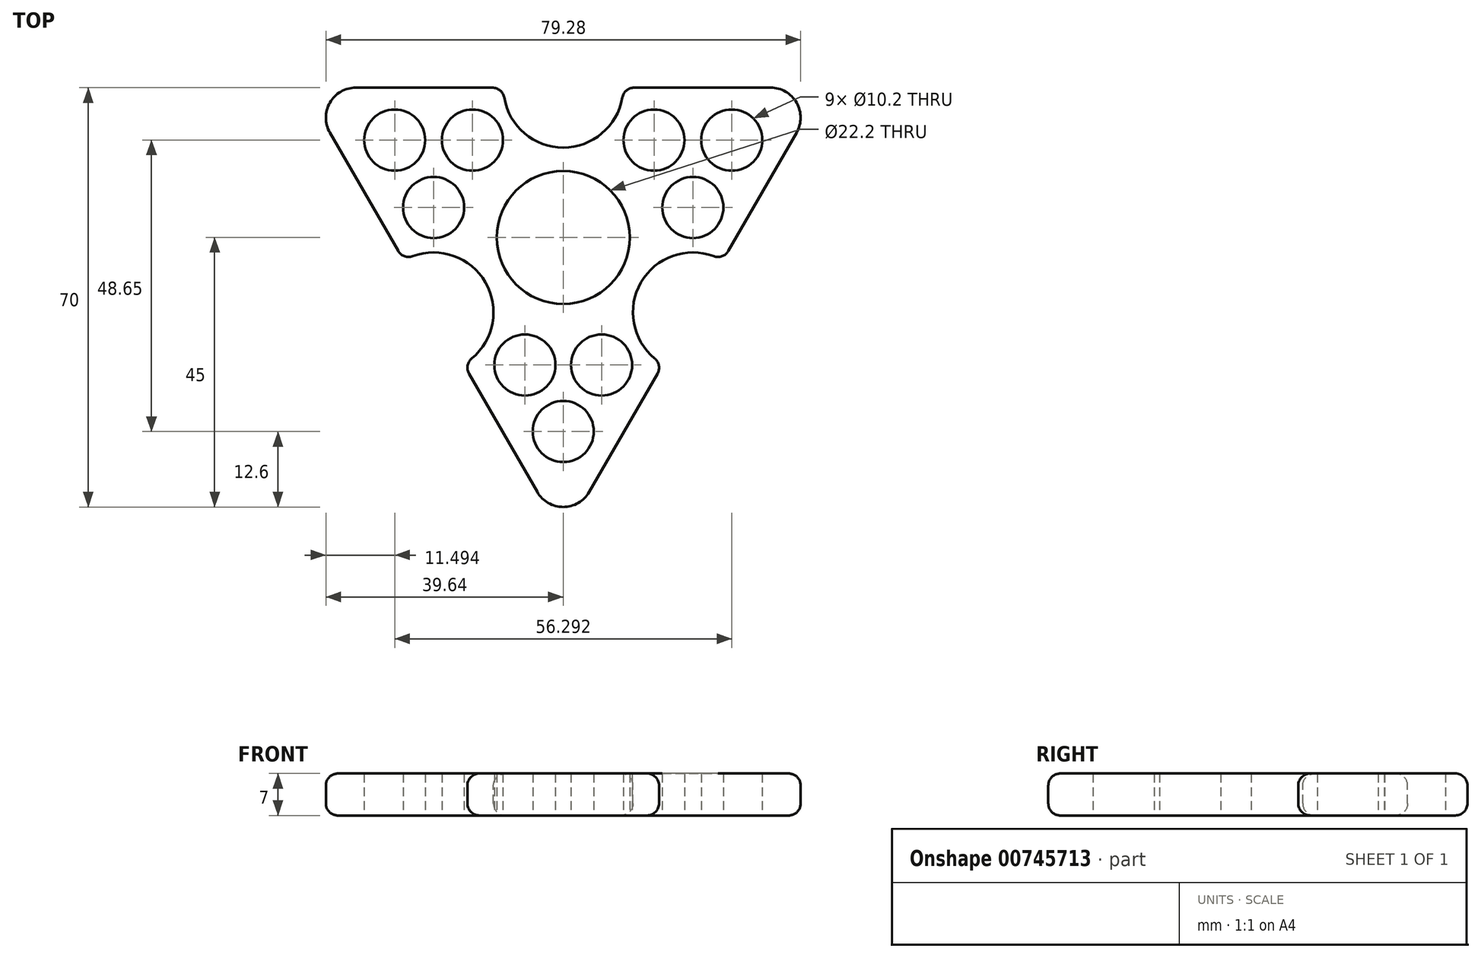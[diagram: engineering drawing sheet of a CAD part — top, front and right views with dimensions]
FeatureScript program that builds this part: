
annotation { "Feature Type Name" : "Feature", "Feature Type Description" : "" }
export const myFeature = defineFeature(function(context is Context, id is Id, definition is map)
    precondition{}
    {
        {
            var Q0;
            Q0=qCreatedBy(makeId("Top.planeOp"),FACE);
            var sketch = newSketch(context, id + "F0", { "sketchPlane" : qUnion([Q0])});
            skCircle(sketch, "E0", {"center": v(0, 0) * mm, "radius": 11.1 * mm});
            skCircle(sketch, "E1", {"center": v(0, -32.4) * mm, "radius": 5.1 * mm});
            skCircle(sketch, "E2.1.0", {"center": v(6.4, -21.3) * mm, "radius": 5.1 * mm});
            skCircle(sketch, "E2.2.0", {"center": v(-6.4, -21.3) * mm, "radius": 5.1 * mm});
            skPoint(sketch, "E2.center", {"position": v(0, -25) * mm});
            skCircle(sketch, "E3.1.1", {"center": v(28.15, 16.25) * mm, "radius": 5.1 * mm});
            skPoint(sketch, "E3.1.2", {"position": v(21.65, 12.5) * mm});
            skCircle(sketch, "E3.1.3", {"center": v(15.16, 16.25) * mm, "radius": 5.1 * mm});
            skCircle(sketch, "E3.1.4", {"center": v(21.65, 5) * mm, "radius": 5.1 * mm});
            skCircle(sketch, "E3.2.1", {"center": v(-28.15, 16.25) * mm, "radius": 5.1 * mm});
            skPoint(sketch, "E3.2.2", {"position": v(-21.65, 12.5) * mm});
            skCircle(sketch, "E3.2.3", {"center": v(-21.65, 5) * mm, "radius": 5.1 * mm});
            skCircle(sketch, "E3.2.4", {"center": v(-15.16, 16.25) * mm, "radius": 5.1 * mm});
            skLineSegment(sketch, "E4", {"start": v(0, 0) * mm, "end": v(0, -37.5) * mm});
            skPoint(sketch, "E5.orphan", {"position": v(0, -45) * mm});
            skPoint(sketch, "E6.orphan", {"position": v(-43.3, 25) * mm});
            skLineSegment(sketch, "E7", {"start": v(0, 0) * mm, "end": v(0, -50) * mm, "construction": true});
            skLineSegment(sketch, "E8", {"start": v(0, 0) * mm, "end": v(-43.3, 25) * mm, "construction": true});
            skLineSegment(sketch, "E9", {"start": v(0, -50) * mm, "end": v(-43.3, 25) * mm});
            skLineSegment(sketch, "E10.1.0", {"start": v(43.3, 25) * mm, "end": v(0, -50) * mm});
            skLineSegment(sketch, "E10.2.0", {"start": v(-43.3, 25) * mm, "end": v(43.3, 25) * mm});
            skSolve(sketch);
        }
        {
            var Q0;
            Q0=makeQuery(id+"F0.imprint","IMPRINT",FACE,{"disambiguationData":[TD([[makeQuery(id+"F0.imprint","IMPRINT",EDGE,{"derivedFrom":sQuery(id+"F0.wireOp",EDGE,"E0")}),-1.0]])]});
            extrude(context, id + "F1", {"entities" : qUnion([Q0]), "depth" : 7 * mm, "offsetDistance" : 25 * mm});
        }
        {
            var Q0;
            Q0=makeQuery(id+"F1.opExtrude","SWEPT_EDGE",EDGE,{"disambiguationData":[OSD([sQuery(id+"F0.wireOp",EDGE,"E9"),sQuery(id+"F0.wireOp",EDGE,"E10.2.0")])]});
            var Q1;
            Q1=makeQuery(id+"F1.opExtrude","SWEPT_EDGE",EDGE,{"disambiguationData":[OSD([sQuery(id+"F0.wireOp",EDGE,"E10.1.0"),sQuery(id+"F0.wireOp",EDGE,"E10.2.0")])]});
            var Q2;
            Q2=makeQuery(id+"F1.opExtrude","SWEPT_EDGE",EDGE,{"disambiguationData":[OSD([sQuery(id+"F0.wireOp",EDGE,"E9"),sQuery(id+"F0.wireOp",EDGE,"E10.1.0")])]});
            fillet(context, id + "F2", {"entities" : qUnion([Q0, Q1, Q2]), "radius" : 5 * mm, "tangentPropagation" : true, "allowEdgeOverflow" : false});
        }
        {
            var Q0;
            Q0=makeQuery(id+"F1.opExtrude","CAP_FACE",FACE,{"disambiguationData":[OSD([sQuery(id+"F0.wireOp",EDGE,"E0"),sQuery(id+"F0.wireOp",EDGE,"E1"),sQuery(id+"F0.wireOp",EDGE,"E2.1.0"),sQuery(id+"F0.wireOp",EDGE,"E2.2.0"),sQuery(id+"F0.wireOp",EDGE,"E3.1.1"),sQuery(id+"F0.wireOp",EDGE,"E3.1.3"),sQuery(id+"F0.wireOp",EDGE,"E3.1.4"),sQuery(id+"F0.wireOp",EDGE,"E3.2.1"),sQuery(id+"F0.wireOp",EDGE,"E3.2.3"),sQuery(id+"F0.wireOp",EDGE,"E3.2.4"),sQuery(id+"F0.wireOp",EDGE,"E9"),sQuery(id+"F0.wireOp",EDGE,"E10.1.0"),sQuery(id+"F0.wireOp",EDGE,"E10.2.0")])],"isStart":false});
            var sketch = newSketch(context, id + "F3", { "sketchPlane" : qUnion([Q0])});
            skCircle(sketch, "E11", {"center": v(0, 25) * mm, "radius": 10 * mm});
            skCircle(sketch, "E12.1.0", {"center": v(-21.65, -12.5) * mm, "radius": 10 * mm});
            skCircle(sketch, "E12.2.0", {"center": v(21.65, -12.5) * mm, "radius": 10 * mm});
            skPoint(sketch, "E12.center", {"position": v(0, 0) * mm});
            skSolve(sketch);
        }
        {
            var Q0;
            {var subQ0=sQuery(id+"F3.wireOp",EDGE,"E11");var subQ1=makeQuery(id+"F1.opExtrude","CAP_EDGE",EDGE,{"disambiguationData":[OSD([sQuery(id+"F0.wireOp",EDGE,"E10.2.0")])],"isStart":false});var subQ2=makeQuery(id+"F3.imprint","INTERSECT",VERTEX,{"disambiguationData":[OD(0.0)],"derivedFrom":[subQ1,subQ0]});Q0=makeQuery(id+"F3.imprint","IMPRINT",FACE,{"disambiguationData":[TD([[makeQuery(id+"F3.imprint","IMPRINT",EDGE,{"disambiguationData":[TD([[subQ2,-1.0]])],"derivedFrom":subQ0}),1.0]])]});}
            var Q1;
            {var subQ0=sQuery(id+"F3.wireOp",EDGE,"E12.1.0");var subQ1=makeQuery(id+"F1.opExtrude","CAP_EDGE",EDGE,{"disambiguationData":[OSD([sQuery(id+"F0.wireOp",EDGE,"E9")])],"isStart":false});var subQ2=makeQuery(id+"F3.imprint","INTERSECT",VERTEX,{"disambiguationData":[OD(0.0)],"derivedFrom":[subQ1,subQ0]});Q1=makeQuery(id+"F3.imprint","IMPRINT",FACE,{"disambiguationData":[TD([[makeQuery(id+"F3.imprint","IMPRINT",EDGE,{"disambiguationData":[TD([[subQ2,-1.0]])],"derivedFrom":subQ0}),1.0]])]});}
            var Q2;
            {var subQ0=sQuery(id+"F3.wireOp",EDGE,"E12.2.0");var subQ1=makeQuery(id+"F1.opExtrude","CAP_EDGE",EDGE,{"disambiguationData":[OSD([sQuery(id+"F0.wireOp",EDGE,"E10.1.0")])],"isStart":false});var subQ2=makeQuery(id+"F3.imprint","INTERSECT",VERTEX,{"disambiguationData":[OD(0.0)],"derivedFrom":[subQ1,subQ0]});Q2=makeQuery(id+"F3.imprint","IMPRINT",FACE,{"disambiguationData":[TD([[makeQuery(id+"F3.imprint","IMPRINT",EDGE,{"disambiguationData":[TD([[subQ2,1.0]])],"derivedFrom":subQ0}),1.0]])]});}
            extrude(context, id + "F4", {"entities" : qUnion([Q0, Q1, Q2]), "operationType" : NewBodyOperationType.REMOVE, "oppositeDirection" : true, "depth" : 25 * mm, "offsetDistance" : 25 * mm});
        }
        {
            var Q0;
            {var subQ0=sQuery(id+"F0.wireOp",EDGE,"E10.1.0");var subQ1=sQuery(id+"F0.wireOp",EDGE,"E9");Q0=makeQuery(id+"F4.boolean.opBoolean","SPLIT",EDGE,{"disambiguationData":[TD([makeQuery(id+"F2.opFillet","BLEND_FACE",FACE,{"disambiguationData":[OSD([subQ1,subQ0])]})])],"derivedFrom":makeQuery(id+"F1.opExtrude","CAP_EDGE",EDGE,{"disambiguationData":[OSD([subQ0])],"isStart":true})});}
            var Q1;
            {var subQ0=sQuery(id+"F0.wireOp",EDGE,"E10.2.0");var subQ1=sQuery(id+"F0.wireOp",EDGE,"E10.1.0");Q1=makeQuery(id+"F4.boolean.opBoolean","SPLIT",EDGE,{"disambiguationData":[TD([makeQuery(id+"F2.opFillet","BLEND_FACE",FACE,{"disambiguationData":[OSD([subQ1,subQ0])]})])],"derivedFrom":makeQuery(id+"F1.opExtrude","CAP_EDGE",EDGE,{"disambiguationData":[OSD([subQ1])],"isStart":true})});}
            var Q2;
            {var subQ0=sQuery(id+"F0.wireOp",EDGE,"E10.2.0");var subQ1=sQuery(id+"F0.wireOp",EDGE,"E9");Q2=makeQuery(id+"F4.boolean.opBoolean","SPLIT",EDGE,{"disambiguationData":[TD([makeQuery(id+"F2.opFillet","BLEND_FACE",FACE,{"disambiguationData":[OSD([subQ1,subQ0])]})])],"derivedFrom":makeQuery(id+"F1.opExtrude","CAP_EDGE",EDGE,{"disambiguationData":[OSD([subQ0])],"isStart":true})});}
            var Q3;
            {var subQ0=sQuery(id+"F0.wireOp",EDGE,"E10.2.0");var subQ1=sQuery(id+"F0.wireOp",EDGE,"E9");Q3=makeQuery(id+"F2.opFillet","BLEND_EDGE",EDGE,{"blendedFrom":[makeQuery(id+"F1.opExtrude","SWEPT_EDGE",EDGE,{"disambiguationData":[OSD([subQ1,subQ0])]}),makeQuery(id+"F1.opExtrude","CAP_FACE",FACE,{"disambiguationData":[OSD([sQuery(id+"F0.wireOp",EDGE,"E0"),sQuery(id+"F0.wireOp",EDGE,"E1"),sQuery(id+"F0.wireOp",EDGE,"E2.1.0"),sQuery(id+"F0.wireOp",EDGE,"E2.2.0"),sQuery(id+"F0.wireOp",EDGE,"E3.1.1"),sQuery(id+"F0.wireOp",EDGE,"E3.1.3"),sQuery(id+"F0.wireOp",EDGE,"E3.1.4"),sQuery(id+"F0.wireOp",EDGE,"E3.2.1"),sQuery(id+"F0.wireOp",EDGE,"E3.2.3"),sQuery(id+"F0.wireOp",EDGE,"E3.2.4"),subQ1,sQuery(id+"F0.wireOp",EDGE,"E10.1.0"),subQ0])],"isStart":false})],"blendedInto":[makeQuery(id+"F1.opExtrude","CAP_FACE",FACE,{"disambiguationData":[OSD([sQuery(id+"F0.wireOp",EDGE,"E0"),sQuery(id+"F0.wireOp",EDGE,"E1"),sQuery(id+"F0.wireOp",EDGE,"E2.1.0"),sQuery(id+"F0.wireOp",EDGE,"E2.2.0"),sQuery(id+"F0.wireOp",EDGE,"E3.1.1"),sQuery(id+"F0.wireOp",EDGE,"E3.1.3"),sQuery(id+"F0.wireOp",EDGE,"E3.1.4"),sQuery(id+"F0.wireOp",EDGE,"E3.2.1"),sQuery(id+"F0.wireOp",EDGE,"E3.2.3"),sQuery(id+"F0.wireOp",EDGE,"E3.2.4"),subQ1,sQuery(id+"F0.wireOp",EDGE,"E10.1.0"),subQ0])],"isStart":false})]});}
            var Q4;
            {var subQ0=sQuery(id+"F0.wireOp",EDGE,"E10.2.0");var subQ1=sQuery(id+"F0.wireOp",EDGE,"E10.1.0");Q4=makeQuery(id+"F2.opFillet","BLEND_EDGE",EDGE,{"blendedFrom":[makeQuery(id+"F1.opExtrude","SWEPT_EDGE",EDGE,{"disambiguationData":[OSD([subQ1,subQ0])]}),makeQuery(id+"F1.opExtrude","CAP_FACE",FACE,{"disambiguationData":[OSD([sQuery(id+"F0.wireOp",EDGE,"E0"),sQuery(id+"F0.wireOp",EDGE,"E1"),sQuery(id+"F0.wireOp",EDGE,"E2.1.0"),sQuery(id+"F0.wireOp",EDGE,"E2.2.0"),sQuery(id+"F0.wireOp",EDGE,"E3.1.1"),sQuery(id+"F0.wireOp",EDGE,"E3.1.3"),sQuery(id+"F0.wireOp",EDGE,"E3.1.4"),sQuery(id+"F0.wireOp",EDGE,"E3.2.1"),sQuery(id+"F0.wireOp",EDGE,"E3.2.3"),sQuery(id+"F0.wireOp",EDGE,"E3.2.4"),sQuery(id+"F0.wireOp",EDGE,"E9"),subQ1,subQ0])],"isStart":false})],"blendedInto":[makeQuery(id+"F1.opExtrude","CAP_FACE",FACE,{"disambiguationData":[OSD([sQuery(id+"F0.wireOp",EDGE,"E0"),sQuery(id+"F0.wireOp",EDGE,"E1"),sQuery(id+"F0.wireOp",EDGE,"E2.1.0"),sQuery(id+"F0.wireOp",EDGE,"E2.2.0"),sQuery(id+"F0.wireOp",EDGE,"E3.1.1"),sQuery(id+"F0.wireOp",EDGE,"E3.1.3"),sQuery(id+"F0.wireOp",EDGE,"E3.1.4"),sQuery(id+"F0.wireOp",EDGE,"E3.2.1"),sQuery(id+"F0.wireOp",EDGE,"E3.2.3"),sQuery(id+"F0.wireOp",EDGE,"E3.2.4"),sQuery(id+"F0.wireOp",EDGE,"E9"),subQ1,subQ0])],"isStart":false})]});}
            var Q5;
            {var subQ0=sQuery(id+"F0.wireOp",EDGE,"E10.1.0");var subQ1=sQuery(id+"F0.wireOp",EDGE,"E9");Q5=makeQuery(id+"F2.opFillet","BLEND_EDGE",EDGE,{"blendedFrom":[makeQuery(id+"F1.opExtrude","SWEPT_EDGE",EDGE,{"disambiguationData":[OSD([subQ1,subQ0])]}),makeQuery(id+"F1.opExtrude","CAP_FACE",FACE,{"disambiguationData":[OSD([sQuery(id+"F0.wireOp",EDGE,"E0"),sQuery(id+"F0.wireOp",EDGE,"E1"),sQuery(id+"F0.wireOp",EDGE,"E2.1.0"),sQuery(id+"F0.wireOp",EDGE,"E2.2.0"),sQuery(id+"F0.wireOp",EDGE,"E3.1.1"),sQuery(id+"F0.wireOp",EDGE,"E3.1.3"),sQuery(id+"F0.wireOp",EDGE,"E3.1.4"),sQuery(id+"F0.wireOp",EDGE,"E3.2.1"),sQuery(id+"F0.wireOp",EDGE,"E3.2.3"),sQuery(id+"F0.wireOp",EDGE,"E3.2.4"),subQ1,subQ0,sQuery(id+"F0.wireOp",EDGE,"E10.2.0")])],"isStart":false})],"blendedInto":[makeQuery(id+"F1.opExtrude","CAP_FACE",FACE,{"disambiguationData":[OSD([sQuery(id+"F0.wireOp",EDGE,"E0"),sQuery(id+"F0.wireOp",EDGE,"E1"),sQuery(id+"F0.wireOp",EDGE,"E2.1.0"),sQuery(id+"F0.wireOp",EDGE,"E2.2.0"),sQuery(id+"F0.wireOp",EDGE,"E3.1.1"),sQuery(id+"F0.wireOp",EDGE,"E3.1.3"),sQuery(id+"F0.wireOp",EDGE,"E3.1.4"),sQuery(id+"F0.wireOp",EDGE,"E3.2.1"),sQuery(id+"F0.wireOp",EDGE,"E3.2.3"),sQuery(id+"F0.wireOp",EDGE,"E3.2.4"),subQ1,subQ0,sQuery(id+"F0.wireOp",EDGE,"E10.2.0")])],"isStart":false})]});}
            fillet(context, id + "F5", {"entities" : qUnion([Q0, Q1, Q2, Q3, Q4, Q5]), "radius" : 2 * mm, "tangentPropagation" : true, "allowEdgeOverflow" : false});
        }
        {
            var Q0;
            Q0=makeQuery(id+"F4.boolean.opBoolean","INTERSECT",EDGE,{"derivedFrom":[makeQuery(id+"F1.opExtrude","CAP_FACE",FACE,{"disambiguationData":[OSD([sQuery(id+"F0.wireOp",EDGE,"E0"),sQuery(id+"F0.wireOp",EDGE,"E1"),sQuery(id+"F0.wireOp",EDGE,"E2.1.0"),sQuery(id+"F0.wireOp",EDGE,"E2.2.0"),sQuery(id+"F0.wireOp",EDGE,"E3.1.1"),sQuery(id+"F0.wireOp",EDGE,"E3.1.3"),sQuery(id+"F0.wireOp",EDGE,"E3.1.4"),sQuery(id+"F0.wireOp",EDGE,"E3.2.1"),sQuery(id+"F0.wireOp",EDGE,"E3.2.3"),sQuery(id+"F0.wireOp",EDGE,"E3.2.4"),sQuery(id+"F0.wireOp",EDGE,"E9"),sQuery(id+"F0.wireOp",EDGE,"E10.1.0"),sQuery(id+"F0.wireOp",EDGE,"E10.2.0")])],"isStart":true}),makeQuery(id+"F4.opExtrude","SWEPT_FACE",FACE,{"disambiguationData":[OSD([sQuery(id+"F3.wireOp",EDGE,"E12.2.0")])]})]});
            var Q1;
            Q1=makeQuery(id+"F4.boolean.opBoolean","INTERSECT",EDGE,{"derivedFrom":[makeQuery(id+"F1.opExtrude","CAP_FACE",FACE,{"disambiguationData":[OSD([sQuery(id+"F0.wireOp",EDGE,"E0"),sQuery(id+"F0.wireOp",EDGE,"E1"),sQuery(id+"F0.wireOp",EDGE,"E2.1.0"),sQuery(id+"F0.wireOp",EDGE,"E2.2.0"),sQuery(id+"F0.wireOp",EDGE,"E3.1.1"),sQuery(id+"F0.wireOp",EDGE,"E3.1.3"),sQuery(id+"F0.wireOp",EDGE,"E3.1.4"),sQuery(id+"F0.wireOp",EDGE,"E3.2.1"),sQuery(id+"F0.wireOp",EDGE,"E3.2.3"),sQuery(id+"F0.wireOp",EDGE,"E3.2.4"),sQuery(id+"F0.wireOp",EDGE,"E9"),sQuery(id+"F0.wireOp",EDGE,"E10.1.0"),sQuery(id+"F0.wireOp",EDGE,"E10.2.0")])],"isStart":true}),makeQuery(id+"F4.opExtrude","SWEPT_FACE",FACE,{"disambiguationData":[OSD([sQuery(id+"F3.wireOp",EDGE,"E12.1.0")])]})]});
            var Q2;
            Q2=makeQuery(id+"F4.boolean.opBoolean","INTERSECT",EDGE,{"derivedFrom":[makeQuery(id+"F1.opExtrude","CAP_FACE",FACE,{"disambiguationData":[OSD([sQuery(id+"F0.wireOp",EDGE,"E0"),sQuery(id+"F0.wireOp",EDGE,"E1"),sQuery(id+"F0.wireOp",EDGE,"E2.1.0"),sQuery(id+"F0.wireOp",EDGE,"E2.2.0"),sQuery(id+"F0.wireOp",EDGE,"E3.1.1"),sQuery(id+"F0.wireOp",EDGE,"E3.1.3"),sQuery(id+"F0.wireOp",EDGE,"E3.1.4"),sQuery(id+"F0.wireOp",EDGE,"E3.2.1"),sQuery(id+"F0.wireOp",EDGE,"E3.2.3"),sQuery(id+"F0.wireOp",EDGE,"E3.2.4"),sQuery(id+"F0.wireOp",EDGE,"E9"),sQuery(id+"F0.wireOp",EDGE,"E10.1.0"),sQuery(id+"F0.wireOp",EDGE,"E10.2.0")])],"isStart":true}),makeQuery(id+"F4.opExtrude","SWEPT_FACE",FACE,{"disambiguationData":[OSD([sQuery(id+"F3.wireOp",EDGE,"E11")])]})]});
            fillet(context, id + "F6", {"entities" : qUnion([Q0, Q1, Q2]), "radius" : 2 * mm, "tangentPropagation" : true, "allowEdgeOverflow" : false});
        }
    });
